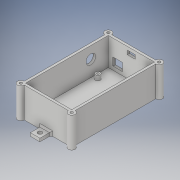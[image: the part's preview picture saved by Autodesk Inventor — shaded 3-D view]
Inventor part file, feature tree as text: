
AUTODESK INVENTOR PART (.ipt)
format: ipt  version: 2019 (Build 230136000, 136)  size: 260,096 bytes
history: native  units: mm
features: extrude x10, sketch x10, projected_geometry x4, mirror x3, chamfer x2
ambient origin geometry x8: Origin, YZ Plane, XZ Plane, XY Plane, X Axis, Y Axis, Z Axis, Center Point
bodies: Solid1 (feature_tree)
feature tree (29):
  extrude  "Extrusion1"  Depth=110.0mm
  extrude  "Extrusion2"  Depth=3.0mm
  extrude  "Extrusion3"  Depth=3.0mm
  extrude  "Extrusion4"  Depth=35.0mm TaperAngle=0.0deg
  extrude  "Extrusion5"  Depth=92.0mm
  extrude  "Extrusion6"  Depth=2.5mm
  extrude  "Extrusion7"  Depth=2.5mm
  mirror  "Mirror1"
  mirror  "Mirror2"
  extrude  "Extrusion8"  Depth=5.92mm
  extrude  "Extrusion9"  Depth=6.0mm
  chamfer  "Chamfer1"  Distance=6.0mm
  extrude  "Extrusion10"  Depth=6.0mm
  mirror  "Mirror3"
  chamfer  "Chamfer2"  Distance=6.0mm
  sketch  "Sketch1"  dims[d0=64.0mm d1=110.0mm]
  sketch  "Sketch2"  dims[d2=3.0mm d3=0.0mm d4=3.0mm]
  projected_geometry  "Projected Loop1"
  sketch  "Sketch3"  dims[d5=3.0mm d6=3.0mm]
  sketch  "Sketch4"  dims[d7=3.0mm d8=35.0mm d9=0.0mm]
  sketch  "Sketch5"  dims[d15=46.16mm d16=92.0mm]
  projected_geometry  "Projected Loop2"
  sketch  "Sketch7"  dims[d17=2.5mm d18=2.5mm]
  projected_geometry  "Projected Loop3"
  sketch  "Sketch8"  dims[d19=2.5mm d20=2.5mm]
  sketch  "Sketch9"  dims[d21=79.0mm d22=5.92mm]
  sketch  "Sketch10"  dims[d23=5.92mm d24=6.0mm]
  sketch  "Sketch11"  dims[d25=6.0mm d26=6.0mm d27=6.0mm d28=6.0mm d29=6.0mm d30=6.0mm d31=0.0mm d33=1.5mm d34=10.0mm d35=12.0mm d36=6.0mm d37=0.0mm d38=20.0mm d39=5.0mm d40=10.0mm d41=24.0mm d42=24.0mm d43=6.0mm d44=0.0mm d45=38.0mm d46=0.0mm d47=3.3mm d48=15.0mm d49=0.0mm d50=12.0mm d51=14.0mm d52=90.0deg d53=3.0mm d54=15.0mm d55=0.0mm d56=4.0mm d57=12.0mm d58=21.757359mm d59=21.757359mm d60=14.0mm d61=0.0mm d62=2.0mm d63=2.0mm d64=45.0deg d65=5.2mm d66=6.0mm d67=6.0mm d68=12.0mm d69=0.0mm d70=2.0mm d71=2.0mm d72=45.0deg]
  projected_geometry  "Projected Loop4"
